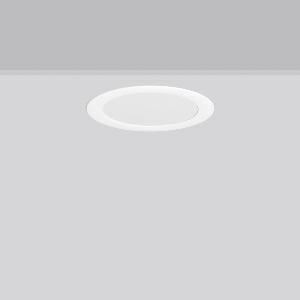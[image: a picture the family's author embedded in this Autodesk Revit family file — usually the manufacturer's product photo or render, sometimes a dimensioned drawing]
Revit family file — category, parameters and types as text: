
# Revit family: toledo_flat_round_672225_002_1_ce67
name_source: partatom
category: Lighting Fixtures
units: mm (PartAtom-declared; Revit-internal decimal feet)

## family parameters
Cut with Voids When Loaded = No
Host = Face
Light Source = No
Part Type = Normal
Room Calculation Point = No
Round Connector Dimension = Use Diameter
Shared = No

## types (1)
- TOLEDO FLAT round (1 x LED Modul 840, 1800 lm, 4000)
    Apparent Load = 17 VA
    Approval mark = CE
    CIE Flux Codes = 48 79 96 100 100
    Color Rendering = 80
    Color Temperature = 4000
    Default Elevation = 1800 mm  [stored 5.90551 ft]
    Description = Series: TOLEDO FLAT round
Ultra thin recessed downlight. For escape route illumination. Housing: die-cast aluminium, powder-coated. Lightguide and diffuser made of non-yellowing plastic (PMMA). Diffuser opal matt plastic. Ceiling installation with spring system. Including separate LED converter with connecting cable 250 mm. Self-contained system with automatic self-test. External driver with simple plug-in locking system. 
Colour: white
Diameter: 255 mm
Height: 3 mm
Cut-out diameter: 234 mm
Recess height: 100 mm
Luminaire: recess height: 60-80 mm
Weight: 1.76 kg
Operating mode: maintained power mode
Duration time: 8 h
Lamp: LED
Socket: without socket
Colour temperature: 4000K
Colour rendering index (CRI): 80
System power: 17 W
Rated luminous flux: 1800 lm
Luminous flux, emergency: 180 lm
System power, emergency: -
Control gear: Regulated power supply
Protection class: I
Type of protection: IP 54
    Height = 0 mm  [stored 0 ft]
    Lamp = 1 x LED Modul 840
    Lamp Light Flux = 1800 lm
    Lamp count = 1
    Length = 255 mm
    Lifetime = 50000 h
    Luminous efficacy = 106 lm/W
    Manufacturer = RZB
    ModVariant = No
    Model = 672225.002.1
    Mounting Place = Ceiling
    Mounting Type = Recessed
    Number of Poles = 1
    OnlyDefault = Yes
    Power Factor = 1
    Product Name = TOLEDO FLAT round
    Product group = Recessed downlights
    ProductGroupID = 402
    Protection Class = Protection class I
    Protection Degree = IP 54
    RLX_Detail_Level = 1
    RLX_Emergency_Light_Flux = 180 lm
    RLX_Emergency_Type = 3
    RLX_Emergency_Type_DB = Yes
    RlxData = <blob elided: 30745 chars, md5=efd788b3>
    Socket = socket
    Standby Power = 0 W
    System Light Flux = 1800 lm
    System Power = 17 W
    Type Comments = Product without accessories
    Type Image = 901453.002.jpg
    URL = http://relux.com
    VarID = ---
    Voltage = 0 V
    Weight = 0.00 kg
    Width = 0 mm  [stored 0 ft]

note: [stored X ft] marks values corroborated as IEEE doubles in the binary element streams (Revit-internal decimal feet)

## geometry (parser evidence)
native form markers: Blend x4, Sweep x11
no freeform markers — native parametric forms only
